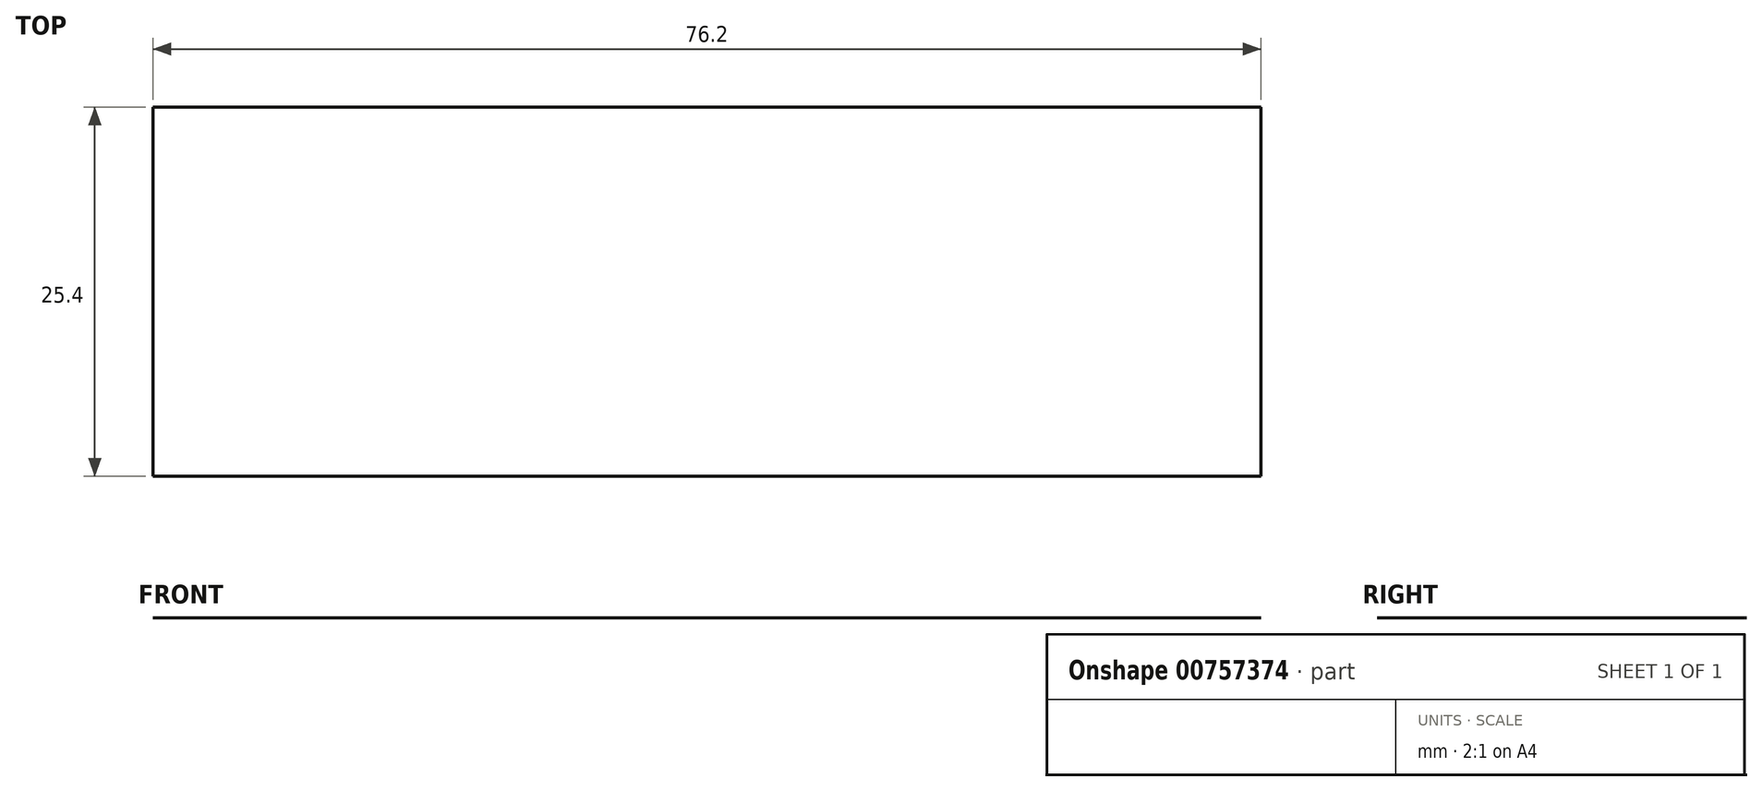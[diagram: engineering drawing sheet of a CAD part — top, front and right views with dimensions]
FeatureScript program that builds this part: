
annotation { "Feature Type Name" : "Feature", "Feature Type Description" : "" }
export const myFeature = defineFeature(function(context is Context, id is Id, definition is map)
    precondition{}
    {
        {
            var Q0;
            Q0=qCreatedBy(makeId("Top.planeOp"),FACE);
            var sketch = newSketch(context, id + "F0", { "sketchPlane" : qUnion([Q0])});
            skLineSegment(sketch, "E0.bottom", {"start": v(-38.1, -12.7) * mm, "end": v(38.1, -12.7) * mm});
            skLineSegment(sketch, "E0.top", {"start": v(-38.1, 12.7) * mm, "end": v(38.1, 12.7) * mm});
            skLineSegment(sketch, "E0.left", {"start": v(-38.1, -12.7) * mm, "end": v(-38.1, 12.7) * mm});
            skLineSegment(sketch, "E0.right", {"start": v(38.1, -12.7) * mm, "end": v(38.1, 12.7) * mm});
            skPoint(sketch, "E0.middle", {"position": v(0, 0) * mm});
            skSolve(sketch);
        }
        {
            var Q0;
            Q0=makeQuery(id+"F0.imprint","IMPRINT",FACE,{"disambiguationData":[TD([[makeQuery(id+"F0.imprint","IMPRINT",EDGE,{"derivedFrom":sQuery(id+"F0.wireOp",EDGE,"E0.bottom")}),1.0]])]});
            extrude(context, id + "F1", {"entities" : qUnion([Q0]), "depth" : 1 / 203.2 * mm, "offsetDistance" : 25.4 * mm});
        }
    });
